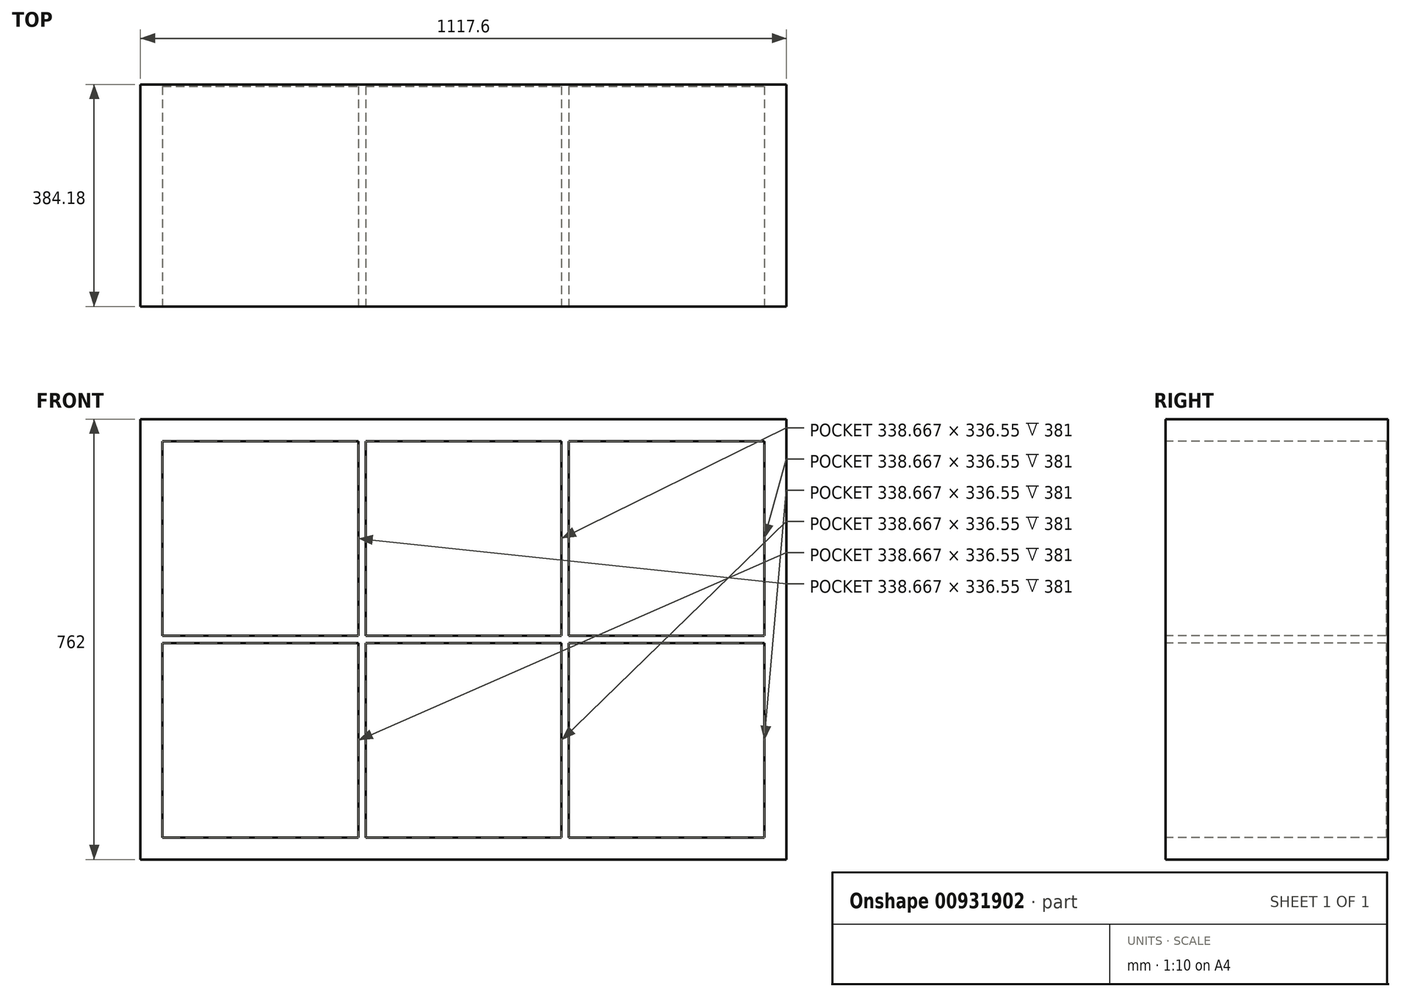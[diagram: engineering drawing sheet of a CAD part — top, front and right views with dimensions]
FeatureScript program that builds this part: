
annotation { "Feature Type Name" : "Feature", "Feature Type Description" : "" }
export const myFeature = defineFeature(function(context is Context, id is Id, definition is map)
    precondition{}
    {
        {
            var Q0;
            Q0=qCreatedBy(makeId("Front.planeOp"),FACE);
            var sketch = newSketch(context, id + "F0", { "sketchPlane" : qUnion([Q0])});
            skLineSegment(sketch, "E0.bottom", {"start": v(0, 0) * mm, "end": v(1117.6, 0) * mm});
            skLineSegment(sketch, "E0.top", {"start": v(0, -762) * mm, "end": v(1117.6, -762) * mm});
            skLineSegment(sketch, "E0.left", {"start": v(0, 0) * mm, "end": v(0, -762) * mm});
            skLineSegment(sketch, "E0.right", {"start": v(1117.6, 0) * mm, "end": v(1117.6, -762) * mm});
            skLineSegment(sketch, "E1.0", {"start": v(38.1, -38.1) * mm, "end": v(376.77, -38.1) * mm});
            skLineSegment(sketch, "E1.1", {"start": v(38.1, -38.1) * mm, "end": v(38.1, -374.65) * mm});
            skLineSegment(sketch, "E1.2", {"start": v(38.1, -723.9) * mm, "end": v(376.77, -723.9) * mm});
            skLineSegment(sketch, "E1.3", {"start": v(1079.5, -38.1) * mm, "end": v(1079.5, -374.65) * mm});
            skLineSegment(sketch, "E2", {"start": v(376.77, -38.1) * mm, "end": v(376.77, -374.65) * mm});
            skLineSegment(sketch, "E3", {"start": v(376.77, -374.65) * mm, "end": v(38.1, -374.65) * mm});
            skLineSegment(sketch, "E4", {"start": v(38.1, -387.35) * mm, "end": v(376.77, -387.35) * mm});
            skLineSegment(sketch, "E5", {"start": v(376.77, -387.35) * mm, "end": v(376.77, -723.9) * mm});
            skLineSegment(sketch, "E6", {"start": v(389.47, -38.1) * mm, "end": v(389.47, -374.65) * mm});
            skLineSegment(sketch, "E7", {"start": v(389.47, -374.65) * mm, "end": v(728.13, -374.65) * mm});
            skLineSegment(sketch, "E8", {"start": v(389.47, -723.9) * mm, "end": v(389.47, -387.35) * mm});
            skLineSegment(sketch, "E9", {"start": v(389.47, -387.35) * mm, "end": v(728.13, -387.35) * mm});
            skLineSegment(sketch, "E10.trimOffspring", {"start": v(38.1, -387.35) * mm, "end": v(38.1, -723.9) * mm});
            skLineSegment(sketch, "E11.trimOffspring", {"start": v(389.47, -38.1) * mm, "end": v(728.13, -38.1) * mm});
            skLineSegment(sketch, "E12.trimOffspring", {"start": v(1079.5, -387.35) * mm, "end": v(1079.5, -723.9) * mm});
            skLineSegment(sketch, "E13.trimOffspring", {"start": v(389.47, -723.9) * mm, "end": v(728.13, -723.9) * mm});
            skLineSegment(sketch, "E14", {"start": v(728.13, -38.1) * mm, "end": v(728.13, -374.65) * mm});
            skLineSegment(sketch, "E15", {"start": v(728.13, -387.35) * mm, "end": v(728.13, -723.9) * mm});
            skLineSegment(sketch, "E16", {"start": v(740.83, -38.1) * mm, "end": v(740.83, -374.65) * mm});
            skLineSegment(sketch, "E17", {"start": v(740.83, -387.35) * mm, "end": v(740.83, -723.9) * mm});
            skLineSegment(sketch, "E18.trimOffspring", {"start": v(740.83, -374.65) * mm, "end": v(1079.5, -374.65) * mm});
            skLineSegment(sketch, "E19.trimOffspring", {"start": v(740.83, -387.35) * mm, "end": v(1079.5, -387.35) * mm});
            skLineSegment(sketch, "E20.trimOffspring", {"start": v(740.83, -38.1) * mm, "end": v(1079.5, -38.1) * mm});
            skLineSegment(sketch, "E21.trimOffspring", {"start": v(740.83, -723.9) * mm, "end": v(1079.5, -723.9) * mm});
            skSolve(sketch);
        }
        {
            var Q0;
            Q0 = qSketchRegion(id + "F0", true);
            extrude(context, id + "F1", {"entities" : qUnion([Q0]), "oppositeDirection" : true, "depth" : 381 * mm, "offsetDistance" : 25.4 * mm});
        }
        {
            var Q0;
            Q0=makeQuery(id+"F1.opExtrude","CAP_FACE",FACE,{"disambiguationData":[OSD([sQuery(id+"F0.wireOp",EDGE,"E0.bottom"),sQuery(id+"F0.wireOp",EDGE,"E0.top"),sQuery(id+"F0.wireOp",EDGE,"E0.left"),sQuery(id+"F0.wireOp",EDGE,"E0.right"),sQuery(id+"F0.wireOp",EDGE,"E1.0"),sQuery(id+"F0.wireOp",EDGE,"E1.1"),sQuery(id+"F0.wireOp",EDGE,"E1.2"),sQuery(id+"F0.wireOp",EDGE,"E1.3"),sQuery(id+"F0.wireOp",EDGE,"E2"),sQuery(id+"F0.wireOp",EDGE,"E3"),sQuery(id+"F0.wireOp",EDGE,"E4"),sQuery(id+"F0.wireOp",EDGE,"E5"),sQuery(id+"F0.wireOp",EDGE,"E6"),sQuery(id+"F0.wireOp",EDGE,"E7"),sQuery(id+"F0.wireOp",EDGE,"E8"),sQuery(id+"F0.wireOp",EDGE,"E9"),sQuery(id+"F0.wireOp",EDGE,"E10.trimOffspring"),sQuery(id+"F0.wireOp",EDGE,"E11.trimOffspring"),sQuery(id+"F0.wireOp",EDGE,"E12.trimOffspring"),sQuery(id+"F0.wireOp",EDGE,"E13.trimOffspring")])],"isStart":false});
            var sketch = newSketch(context, id + "F2", { "sketchPlane" : qUnion([Q0])});
            skLineSegment(sketch, "E22.bottom", {"start": v(-1117.6, 0) * mm, "end": v(0, 0) * mm});
            skLineSegment(sketch, "E22.top", {"start": v(-1117.6, -762) * mm, "end": v(0, -762) * mm});
            skLineSegment(sketch, "E22.left", {"start": v(-1117.6, 0) * mm, "end": v(-1117.6, -762) * mm});
            skLineSegment(sketch, "E22.right", {"start": v(0, 0) * mm, "end": v(0, -762) * mm});
            skSolve(sketch);
        }
        {
            var Q0;
            Q0 = qSketchRegion(id + "F2", true);
            extrude(context, id + "F3", {"entities" : qUnion([Q0]), "operationType" : NewBodyOperationType.ADD, "depth" : 3.17 * mm, "offsetDistance" : 25.4 * mm});
        }
    });
